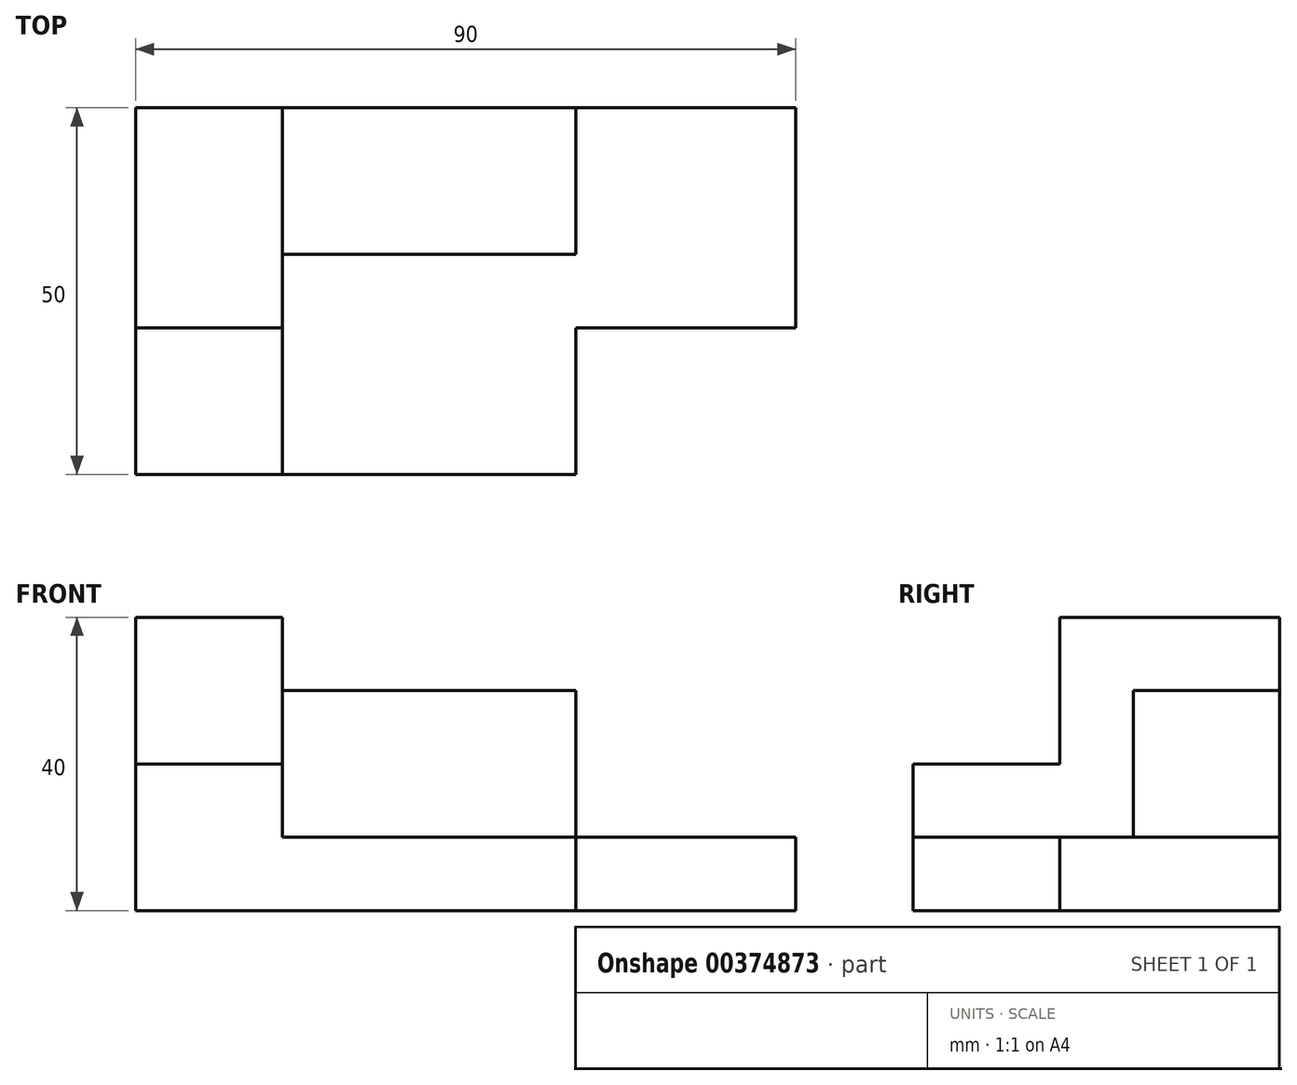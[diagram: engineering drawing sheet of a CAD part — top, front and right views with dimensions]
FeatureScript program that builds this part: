
annotation { "Feature Type Name" : "Feature", "Feature Type Description" : "" }
export const myFeature = defineFeature(function(context is Context, id is Id, definition is map)
    precondition{}
    {
        {
            var Q0;
            Q0=qCreatedBy(makeId("Top.planeOp"),FACE);
            var sketch = newSketch(context, id + "F0", { "sketchPlane" : qUnion([Q0])});
            skLineSegment(sketch, "E0", {"start": v(-51.67, -40.27) * mm, "end": v(8.33, -40.27) * mm});
            skLineSegment(sketch, "E1", {"start": v(8.33, -40.27) * mm, "end": v(8.33, -20.27) * mm});
            skLineSegment(sketch, "E2", {"start": v(8.33, -20.27) * mm, "end": v(38.33, -20.27) * mm});
            skLineSegment(sketch, "E3", {"start": v(38.33, -20.27) * mm, "end": v(38.33, 9.73) * mm});
            skLineSegment(sketch, "E4", {"start": v(38.33, 9.73) * mm, "end": v(-51.67, 9.73) * mm});
            skLineSegment(sketch, "E5", {"start": v(-51.67, -40.27) * mm, "end": v(-51.67, 9.73) * mm});
            skSolve(sketch);
        }
        {
            var Q0;
            Q0=makeQuery(id+"F0.imprint","IMPRINT",FACE,{"disambiguationData":[TD([[makeQuery(id+"F0.imprint","IMPRINT",EDGE,{"derivedFrom":sQuery(id+"F0.wireOp",EDGE,"E0")}),1.0]])]});
            extrude(context, id + "F1", {"entities" : qUnion([Q0]), "depth" : 10 * mm});
        }
        {
            var Q0;
            Q0=makeQuery(id+"F1.opExtrude","SWEPT_FACE",FACE,{"disambiguationData":[OSD([sQuery(id+"F0.wireOp",EDGE,"E5")])]});
            var sketch = newSketch(context, id + "F2", { "sketchPlane" : qUnion([Q0])});
            skLineSegment(sketch, "E6", {"start": v(-9.73, 0) * mm, "end": v(-9.73, 40) * mm});
            skLineSegment(sketch, "E7", {"start": v(-9.73, 40) * mm, "end": v(20.27, 40) * mm});
            skLineSegment(sketch, "E8", {"start": v(20.27, 40) * mm, "end": v(20.27, 20) * mm});
            skLineSegment(sketch, "E9", {"start": v(20.27, 20) * mm, "end": v(40.27, 20) * mm});
            skLineSegment(sketch, "E10", {"start": v(40.27, 20) * mm, "end": v(40.27, 0) * mm});
            skLineSegment(sketch, "E11", {"start": v(40.27, 0) * mm, "end": v(-9.73, 0) * mm});
            skSolve(sketch);
        }
        {
            var Q0;
            {var subQ1=sQuery(id+"F2.wireOp",EDGE,"E7");Q0=makeQuery(id+"F2.imprint","IMPRINT",FACE,{"disambiguationData":[TD([[makeQuery(id+"F2.imprint","IMPRINT",EDGE,{"derivedFrom":subQ1}),-1.0]])]});}
            extrude(context, id + "F3", {"entities" : qUnion([Q0]), "operationType" : NewBodyOperationType.ADD, "oppositeDirection" : true, "depth" : 20 * mm});
        }
        {
            var Q0;
            Q0=makeQuery(id+"F1.opExtrude","CAP_FACE",FACE,{"disambiguationData":[OSD([sQuery(id+"F0.wireOp",EDGE,"E0"),sQuery(id+"F0.wireOp",EDGE,"E1"),sQuery(id+"F0.wireOp",EDGE,"E2"),sQuery(id+"F0.wireOp",EDGE,"E3"),sQuery(id+"F0.wireOp",EDGE,"E4"),sQuery(id+"F0.wireOp",EDGE,"E5")])],"isStart":false});
            var sketch = newSketch(context, id + "F4", { "sketchPlane" : qUnion([Q0])});
            skLineSegment(sketch, "E12", {"start": v(-31.67, 9.73) * mm, "end": v(8.33, 9.73) * mm});
            skLineSegment(sketch, "E13", {"start": v(8.33, 9.73) * mm, "end": v(8.33, -10.27) * mm});
            skLineSegment(sketch, "E14", {"start": v(8.33, -10.27) * mm, "end": v(-31.67, -10.27) * mm});
            skLineSegment(sketch, "E15", {"start": v(-31.67, -10.27) * mm, "end": v(-31.67, 9.73) * mm});
            skSolve(sketch);
        }
        {
            var Q0;
            Q0=makeQuery(id+"F4.imprint","IMPRINT",FACE,{"disambiguationData":[TD([[makeQuery(id+"F4.imprint","IMPRINT",EDGE,{"derivedFrom":sQuery(id+"F4.wireOp",EDGE,"E12")}),1.0]])]});
            extrude(context, id + "F5", {"entities" : qUnion([Q0]), "operationType" : NewBodyOperationType.ADD, "depth" : 20 * mm});
        }
    });
